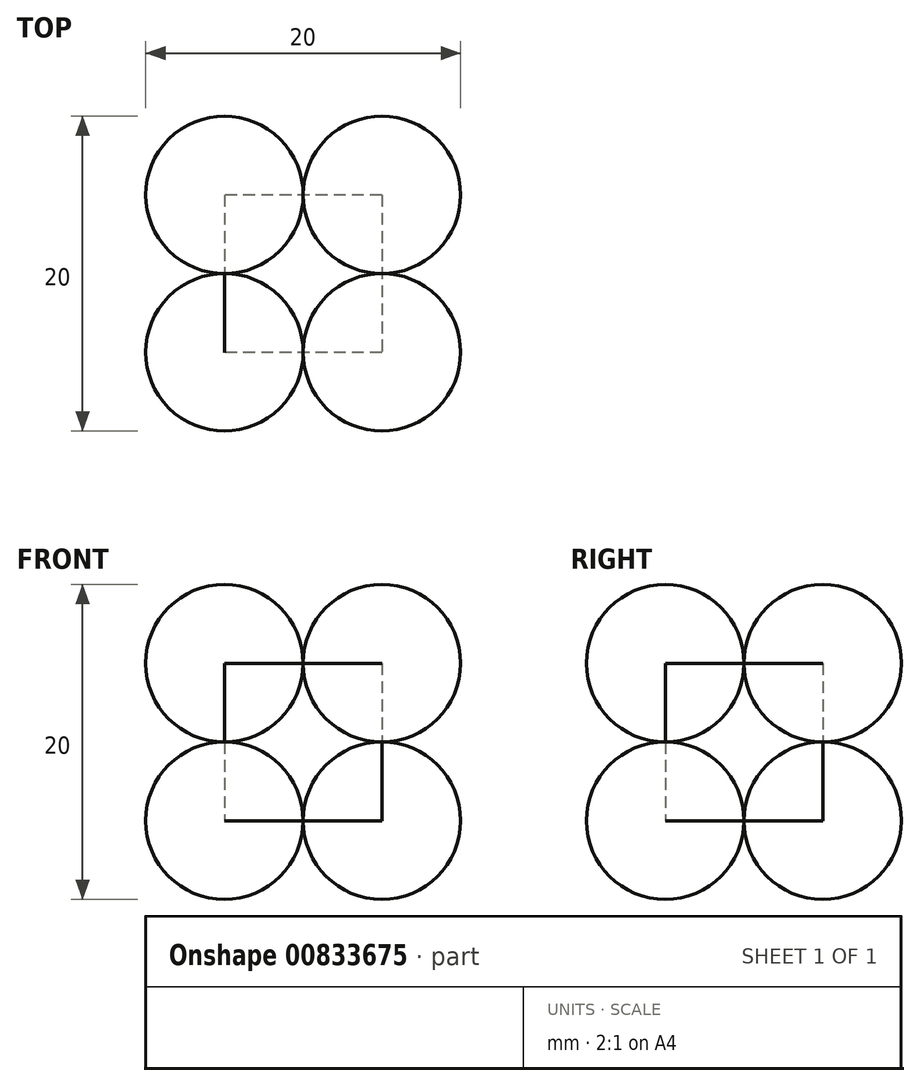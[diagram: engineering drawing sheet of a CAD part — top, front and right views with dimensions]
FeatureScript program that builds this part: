
annotation { "Feature Type Name" : "Feature", "Feature Type Description" : "" }
export const myFeature = defineFeature(function(context is Context, id is Id, definition is map)
    precondition{}
    {
        {
            var Q0;
            Q0=qCreatedBy(makeId("Top.planeOp"),FACE);
            var sketch = newSketch(context, id + "F0", { "sketchPlane" : qUnion([Q0])});
            skLineSegment(sketch, "E0.bottom", {"start": v(5, 5) * mm, "end": v(-5, 5) * mm});
            skLineSegment(sketch, "E0.top", {"start": v(5, -5) * mm, "end": v(-5, -5) * mm});
            skLineSegment(sketch, "E0.left", {"start": v(5, 5) * mm, "end": v(5, -5) * mm});
            skLineSegment(sketch, "E0.right", {"start": v(-5, 5) * mm, "end": v(-5, -5) * mm});
            skPoint(sketch, "E0.middle", {"position": v(0, 0) * mm});
            skSolve(sketch);
        }
        {
            var Q0;
            Q0=makeQuery(id+"F0.imprint","IMPRINT",FACE,{"disambiguationData":[TD([[makeQuery(id+"F0.imprint","IMPRINT",EDGE,{"derivedFrom":sQuery(id+"F0.wireOp",EDGE,"E0.bottom")}),1.0]])]});
            extrude(context, id + "F1", {"entities" : qUnion([Q0]), "depth" : 5 * mm, "offsetDistance" : 25 * mm, "hasSecondDirection" : true, "secondDirectionOppositeDirection" : true, "secondDirectionDepth" : 5 * mm});
        }
        {
            var Q0;
            Q0=makeQuery(id+"F1.opExtrude","CAP_FACE",FACE,{"disambiguationData":[OSD([sQuery(id+"F0.wireOp",EDGE,"E0.bottom"),sQuery(id+"F0.wireOp",EDGE,"E0.top"),sQuery(id+"F0.wireOp",EDGE,"E0.left"),sQuery(id+"F0.wireOp",EDGE,"E0.right")])],"isStart":false});
            var sketch = newSketch(context, id + "F2", { "sketchPlane" : qUnion([Q0])});
            skCircle(sketch, "E1", {"center": v(5, 5) * mm, "radius": 5 * mm});
            skCircle(sketch, "E2", {"center": v(-5, 5) * mm, "radius": 5 * mm});
            skCircle(sketch, "E3", {"center": v(5, -5) * mm, "radius": 5 * mm});
            skCircle(sketch, "E4", {"center": v(-5, -5) * mm, "radius": 5 * mm});
            skLineSegment(sketch, "E5", {"start": v(0, 0) * mm, "end": v(-8.54, 8.54) * mm});
            skLineSegment(sketch, "E6", {"start": v(0, 0) * mm, "end": v(8.54, 8.54) * mm});
            skLineSegment(sketch, "E7", {"start": v(0, 0) * mm, "end": v(8.54, -8.54) * mm});
            skLineSegment(sketch, "E8", {"start": v(0, 0) * mm, "end": v(-8.54, -8.54) * mm});
            skSolve(sketch);
        }
        {
            var Q0;
            {var subQ0=sQuery(id+"F2.wireOp",EDGE,"E6");var subQ1=sQuery(id+"F2.wireOp",EDGE,"E1");var subQ2=makeQuery(id+"F2.imprint","INTERSECT",VERTEX,{"disambiguationData":[OD(1.0)],"derivedFrom":[subQ1,subQ0]});Q0=makeQuery(id+"F2.imprint","IMPRINT",FACE,{"disambiguationData":[TD([[makeQuery(id+"F2.imprint","IMPRINT",EDGE,{"disambiguationData":[TD([[subQ2,-1.0]])],"derivedFrom":subQ1}),1.0]])]});}
            var Q1;
            {var subQ0=sQuery(id+"F2.wireOp",EDGE,"E6");var subQ1=sQuery(id+"F2.wireOp",EDGE,"E1");var subQ2=makeQuery(id+"F2.imprint","INTERSECT",VERTEX,{"disambiguationData":[OD(0.0)],"derivedFrom":[subQ1,subQ0]});Q1=makeQuery(id+"F2.imprint","IMPRINT",FACE,{"disambiguationData":[TD([[makeQuery(id+"F2.imprint","IMPRINT",EDGE,{"disambiguationData":[TD([[subQ2,1.0]])],"derivedFrom":subQ1}),1.0]])]});}
            var Q2;
            Q2=sQuery(id+"F2.wireOp",EDGE,"E6");
            revolve(context, id + "F3", {"surfaceOperationType" : NewSurfaceOperationType.NEW, "entities" : qUnion([Q0, Q1]), "axis" : qUnion([Q2]), "revolveType" : RevolveType.FULL});
        }
        {
            var Q0;
            {var subQ0=sQuery(id+"F2.wireOp",EDGE,"E5");var subQ1=sQuery(id+"F2.wireOp",EDGE,"E2");var subQ2=makeQuery(id+"F2.imprint","INTERSECT",VERTEX,{"disambiguationData":[OD(0.0)],"derivedFrom":[subQ1,subQ0]});Q0=makeQuery(id+"F2.imprint","IMPRINT",FACE,{"disambiguationData":[TD([[makeQuery(id+"F2.imprint","IMPRINT",EDGE,{"disambiguationData":[TD([[subQ2,-1.0]])],"derivedFrom":subQ1}),1.0]])]});}
            var Q1;
            {var subQ0=sQuery(id+"F2.wireOp",EDGE,"E5");var subQ1=sQuery(id+"F2.wireOp",EDGE,"E2");var subQ2=makeQuery(id+"F2.imprint","INTERSECT",VERTEX,{"disambiguationData":[OD(1.0)],"derivedFrom":[subQ1,subQ0]});Q1=makeQuery(id+"F2.imprint","IMPRINT",FACE,{"disambiguationData":[TD([[makeQuery(id+"F2.imprint","IMPRINT",EDGE,{"disambiguationData":[TD([[subQ2,1.0]])],"derivedFrom":subQ1}),1.0]])]});}
            var Q2;
            Q2=sQuery(id+"F2.wireOp",EDGE,"E5");
            revolve(context, id + "F4", {"surfaceOperationType" : NewSurfaceOperationType.NEW, "entities" : qUnion([Q0, Q1]), "axis" : qUnion([Q2]), "revolveType" : RevolveType.FULL});
        }
        {
            var Q0;
            {var subQ0=sQuery(id+"F2.wireOp",EDGE,"E8");var subQ1=sQuery(id+"F2.wireOp",EDGE,"E4");var subQ2=makeQuery(id+"F2.imprint","INTERSECT",VERTEX,{"disambiguationData":[OD(0.0)],"derivedFrom":[subQ1,subQ0]});Q0=makeQuery(id+"F2.imprint","IMPRINT",FACE,{"disambiguationData":[TD([[makeQuery(id+"F2.imprint","IMPRINT",EDGE,{"disambiguationData":[TD([[subQ2,1.0]])],"derivedFrom":subQ1}),1.0]])]});}
            var Q1;
            {var subQ0=sQuery(id+"F2.wireOp",EDGE,"E8");var subQ1=sQuery(id+"F2.wireOp",EDGE,"E4");var subQ2=makeQuery(id+"F2.imprint","INTERSECT",VERTEX,{"disambiguationData":[OD(1.0)],"derivedFrom":[subQ1,subQ0]});Q1=makeQuery(id+"F2.imprint","IMPRINT",FACE,{"disambiguationData":[TD([[makeQuery(id+"F2.imprint","IMPRINT",EDGE,{"disambiguationData":[TD([[subQ2,-1.0]])],"derivedFrom":subQ1}),1.0]])]});}
            var Q2;
            Q2=sQuery(id+"F2.wireOp",EDGE,"E8");
            revolve(context, id + "F5", {"surfaceOperationType" : NewSurfaceOperationType.NEW, "entities" : qUnion([Q0, Q1]), "axis" : qUnion([Q2]), "revolveType" : RevolveType.FULL});
        }
        {
            var Q0;
            {var subQ0=sQuery(id+"F2.wireOp",EDGE,"E7");var subQ1=sQuery(id+"F2.wireOp",EDGE,"E3");var subQ2=makeQuery(id+"F2.imprint","INTERSECT",VERTEX,{"disambiguationData":[OD(0.0)],"derivedFrom":[subQ1,subQ0]});Q0=makeQuery(id+"F2.imprint","IMPRINT",FACE,{"disambiguationData":[TD([[makeQuery(id+"F2.imprint","IMPRINT",EDGE,{"disambiguationData":[TD([[subQ2,-1.0]])],"derivedFrom":subQ1}),1.0]])]});}
            var Q1;
            {var subQ0=sQuery(id+"F2.wireOp",EDGE,"E7");var subQ1=sQuery(id+"F2.wireOp",EDGE,"E3");var subQ2=makeQuery(id+"F2.imprint","INTERSECT",VERTEX,{"disambiguationData":[OD(1.0)],"derivedFrom":[subQ1,subQ0]});Q1=makeQuery(id+"F2.imprint","IMPRINT",FACE,{"disambiguationData":[TD([[makeQuery(id+"F2.imprint","IMPRINT",EDGE,{"disambiguationData":[TD([[subQ2,1.0]])],"derivedFrom":subQ1}),1.0]])]});}
            var Q2;
            Q2=sQuery(id+"F2.wireOp",EDGE,"E7");
            revolve(context, id + "F6", {"surfaceOperationType" : NewSurfaceOperationType.NEW, "entities" : qUnion([Q0, Q1]), "axis" : qUnion([Q2]), "revolveType" : RevolveType.FULL});
        }
        {
            var Q0;
            Q0=makeQuery(id+"F1.opExtrude","CAP_FACE",FACE,{"disambiguationData":[OSD([sQuery(id+"F0.wireOp",EDGE,"E0.bottom"),sQuery(id+"F0.wireOp",EDGE,"E0.top"),sQuery(id+"F0.wireOp",EDGE,"E0.left"),sQuery(id+"F0.wireOp",EDGE,"E0.right")])],"isStart":true});
            var sketch = newSketch(context, id + "F7", { "sketchPlane" : qUnion([Q0])});
            skCircle(sketch, "E9", {"center": v(-5, 5) * mm, "radius": 5 * mm});
            skCircle(sketch, "E10", {"center": v(5, 5) * mm, "radius": 5 * mm});
            skCircle(sketch, "E11", {"center": v(5, -5) * mm, "radius": 5 * mm});
            skCircle(sketch, "E12", {"center": v(-5, -5) * mm, "radius": 5 * mm});
            skLineSegment(sketch, "E13", {"start": v(-10.13, 10.13) * mm, "end": v(10.48, -10.48) * mm});
            skLineSegment(sketch, "E14", {"start": v(-10.9, -10.9) * mm, "end": v(9.64, 9.64) * mm});
            skSolve(sketch);
        }
        {
            var Q0;
            {var subQ0=sQuery(id+"F7.wireOp",EDGE,"E13");var subQ1=sQuery(id+"F7.wireOp",EDGE,"E9");var subQ2=makeQuery(id+"F7.imprint","INTERSECT",VERTEX,{"disambiguationData":[OD(0.0)],"derivedFrom":[subQ1,subQ0]});Q0=makeQuery(id+"F7.imprint","IMPRINT",FACE,{"disambiguationData":[TD([[makeQuery(id+"F7.imprint","IMPRINT",EDGE,{"disambiguationData":[TD([[subQ2,1.0]])],"derivedFrom":subQ1}),1.0]])]});}
            var Q1;
            {var subQ0=sQuery(id+"F7.wireOp",EDGE,"E13");var subQ1=sQuery(id+"F7.wireOp",EDGE,"E9");var subQ2=makeQuery(id+"F7.imprint","INTERSECT",VERTEX,{"disambiguationData":[OD(1.0)],"derivedFrom":[subQ1,subQ0]});Q1=makeQuery(id+"F7.imprint","IMPRINT",FACE,{"disambiguationData":[TD([[makeQuery(id+"F7.imprint","IMPRINT",EDGE,{"disambiguationData":[TD([[subQ2,-1.0]])],"derivedFrom":subQ1}),1.0]])]});}
            var Q2;
            Q2=sQuery(id+"F7.wireOp",EDGE,"E13");
            revolve(context, id + "F8", {"surfaceOperationType" : NewSurfaceOperationType.NEW, "entities" : qUnion([Q0, Q1]), "axis" : qUnion([Q2]), "revolveType" : RevolveType.FULL});
        }
        {
            var Q0;
            {var subQ0=sQuery(id+"F7.wireOp",EDGE,"E14");var subQ1=sQuery(id+"F7.wireOp",EDGE,"E10");var subQ2=makeQuery(id+"F7.imprint","INTERSECT",VERTEX,{"disambiguationData":[OD(0.0)],"derivedFrom":[subQ1,subQ0]});Q0=makeQuery(id+"F7.imprint","IMPRINT",FACE,{"disambiguationData":[TD([[makeQuery(id+"F7.imprint","IMPRINT",EDGE,{"disambiguationData":[TD([[subQ2,-1.0]])],"derivedFrom":subQ1}),1.0]])]});}
            var Q1;
            {var subQ0=sQuery(id+"F7.wireOp",EDGE,"E14");var subQ1=sQuery(id+"F7.wireOp",EDGE,"E10");var subQ2=makeQuery(id+"F7.imprint","INTERSECT",VERTEX,{"disambiguationData":[OD(1.0)],"derivedFrom":[subQ1,subQ0]});Q1=makeQuery(id+"F7.imprint","IMPRINT",FACE,{"disambiguationData":[TD([[makeQuery(id+"F7.imprint","IMPRINT",EDGE,{"disambiguationData":[TD([[subQ2,1.0]])],"derivedFrom":subQ1}),1.0]])]});}
            var Q2;
            Q2=sQuery(id+"F7.wireOp",EDGE,"E14");
            revolve(context, id + "F9", {"surfaceOperationType" : NewSurfaceOperationType.NEW, "entities" : qUnion([Q0, Q1]), "axis" : qUnion([Q2]), "revolveType" : RevolveType.FULL});
        }
        {
            var Q0;
            {var subQ0=sQuery(id+"F7.wireOp",EDGE,"E13");var subQ1=sQuery(id+"F7.wireOp",EDGE,"E11");var subQ2=makeQuery(id+"F7.imprint","INTERSECT",VERTEX,{"disambiguationData":[OD(0.0)],"derivedFrom":[subQ1,subQ0]});Q0=makeQuery(id+"F7.imprint","IMPRINT",FACE,{"disambiguationData":[TD([[makeQuery(id+"F7.imprint","IMPRINT",EDGE,{"disambiguationData":[TD([[subQ2,-1.0]])],"derivedFrom":subQ1}),1.0]])]});}
            var Q1;
            {var subQ0=sQuery(id+"F7.wireOp",EDGE,"E13");var subQ1=sQuery(id+"F7.wireOp",EDGE,"E11");var subQ2=makeQuery(id+"F7.imprint","INTERSECT",VERTEX,{"disambiguationData":[OD(1.0)],"derivedFrom":[subQ1,subQ0]});Q1=makeQuery(id+"F7.imprint","IMPRINT",FACE,{"disambiguationData":[TD([[makeQuery(id+"F7.imprint","IMPRINT",EDGE,{"disambiguationData":[TD([[subQ2,1.0]])],"derivedFrom":subQ1}),1.0]])]});}
            var Q2;
            Q2=sQuery(id+"F7.wireOp",EDGE,"E13");
            revolve(context, id + "F10", {"surfaceOperationType" : NewSurfaceOperationType.NEW, "entities" : qUnion([Q0, Q1]), "axis" : qUnion([Q2]), "revolveType" : RevolveType.FULL});
        }
        {
            var Q0;
            {var subQ0=sQuery(id+"F7.wireOp",EDGE,"E14");var subQ1=sQuery(id+"F7.wireOp",EDGE,"E12");var subQ2=makeQuery(id+"F7.imprint","INTERSECT",VERTEX,{"disambiguationData":[OD(0.0)],"derivedFrom":[subQ1,subQ0]});Q0=makeQuery(id+"F7.imprint","IMPRINT",FACE,{"disambiguationData":[TD([[makeQuery(id+"F7.imprint","IMPRINT",EDGE,{"disambiguationData":[TD([[subQ2,1.0]])],"derivedFrom":subQ1}),1.0]])]});}
            var Q1;
            {var subQ0=sQuery(id+"F7.wireOp",EDGE,"E14");var subQ1=sQuery(id+"F7.wireOp",EDGE,"E12");var subQ2=makeQuery(id+"F7.imprint","INTERSECT",VERTEX,{"disambiguationData":[OD(1.0)],"derivedFrom":[subQ1,subQ0]});Q1=makeQuery(id+"F7.imprint","IMPRINT",FACE,{"disambiguationData":[TD([[makeQuery(id+"F7.imprint","IMPRINT",EDGE,{"disambiguationData":[TD([[subQ2,-1.0]])],"derivedFrom":subQ1}),1.0]])]});}
            var Q2;
            Q2=sQuery(id+"F7.wireOp",EDGE,"E14");
            revolve(context, id + "F11", {"surfaceOperationType" : NewSurfaceOperationType.NEW, "entities" : qUnion([Q0, Q1]), "axis" : qUnion([Q2]), "revolveType" : RevolveType.FULL});
        }
    });
